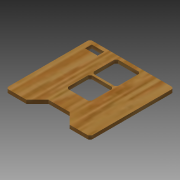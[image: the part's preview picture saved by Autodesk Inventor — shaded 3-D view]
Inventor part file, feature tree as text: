
AUTODESK INVENTOR PART (.ipt)
format: ipt  version: 2013 (Build 170138000, 138)  size: 162,304 bytes
history: native  units: in
note: dims shown in document units (in); Inventor stores cm internally (conversion verified against a paired STEP export)
features: extrude x3, chamfer x3, sketch x3
ambient origin geometry x8: Origin, YZ Plane, XZ Plane, XY Plane, X Axis, Y Axis, Z Axis, Center Point
bodies: Solid1 (feature_tree)
feature tree (9):
  extrude  "Extrusion1"  Depth=6.0in
  chamfer  "Chamfer2"  Distance=1.75in
  chamfer  "Chamfer3"  Distance=1.75in
  extrude  "Extrusion2"  Depth=0.875in
  chamfer  "Chamfer4"  Distance=0.25in
  extrude  "Extrusion3"  Depth=2.2126in
  sketch  "Sketch1"  dims[d0=6.0in d2=6.0in]
  sketch  "Sketch3"  dims[d3=3.0in]
  sketch  "Sketch4"  dims[d4=3.0in d5=1.75in d6=1.75in d7=0.875in d9=0.25in d10=0.0in d26=2.2126in d31=45.0deg d32=45.0deg d33=1.5in d34=2.25in d35=0.125in d36=0.125in d37=45.0deg d38=0.125in d39=0.125in d40=45.0deg d41=1.7in d43=1.7in d44=0.85in d45=0.85in d46=0.125in d47=0.125in d48=0.125in d49=0.125in d50=0.125in d51=0.125in d52=0.125in d53=0.125in d54=1.0in d55=0.0in d56=0.25in d57=0.125in d58=0.125in d59=45.0deg d60=0.475in d62=0.9in d65=0.375in d66=0.25in d67=1.0in d68=0.0in]
